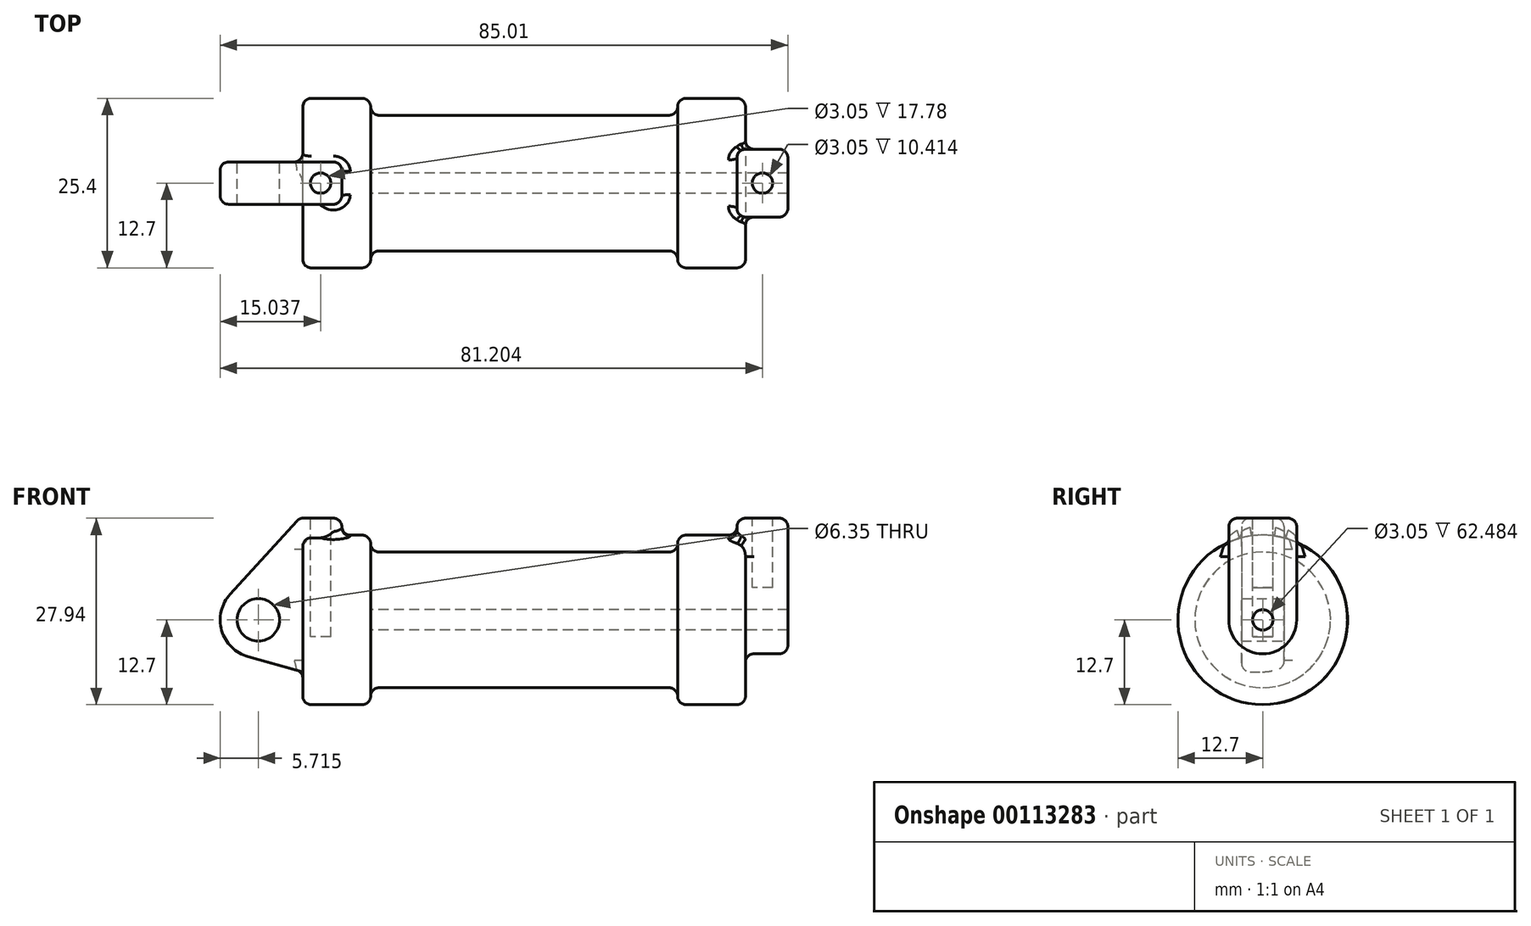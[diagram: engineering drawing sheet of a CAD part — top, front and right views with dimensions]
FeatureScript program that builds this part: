
annotation { "Feature Type Name" : "Feature", "Feature Type Description" : "" }
export const myFeature = defineFeature(function(context is Context, id is Id, definition is map)
    precondition{}
    {
        {
            var Q0;
            Q0=qCreatedBy(makeId("Front.planeOp"),FACE);
            var sketch = newSketch(context, id + "F0", { "sketchPlane" : qUnion([Q0])});
            skLineSegment(sketch, "E0", {"start": v(0, 0) * mm, "end": v(0, 12.7) * mm});
            skLineSegment(sketch, "E1", {"start": v(0, 12.7) * mm, "end": v(10.16, 12.7) * mm});
            skLineSegment(sketch, "E2", {"start": v(10.16, 12.7) * mm, "end": v(10.16, 10.16) * mm});
            skLineSegment(sketch, "E3", {"start": v(10.16, 10.16) * mm, "end": v(56.13, 10.16) * mm});
            skLineSegment(sketch, "E4", {"start": v(56.13, 10.16) * mm, "end": v(56.13, 12.7) * mm});
            skLineSegment(sketch, "E5", {"start": v(56.13, 12.7) * mm, "end": v(66.3, 12.7) * mm});
            skLineSegment(sketch, "E6", {"start": v(66.3, 12.7) * mm, "end": v(66.3, 0) * mm});
            skLineSegment(sketch, "E7", {"start": v(66.3, 0) * mm, "end": v(0, 0) * mm});
            skLineSegment(sketch, "E8", {"start": v(5.84, 15.24) * mm, "end": v(-0.5, 15.24) * mm});
            skLineSegment(sketch, "E9", {"start": v(-0.5, 15.24) * mm, "end": v(-10.88, 3.85) * mm});
            skLineSegment(sketch, "E10", {"start": v(0, 0) * mm, "end": v(-6.65, 0) * mm});
            skCircle(sketch, "E11", {"center": v(-6.65, 0) * mm, "radius": 5.72 * mm});
            skCircle(sketch, "E12", {"center": v(-6.65, 0) * mm, "radius": 3.18 * mm});
            skLineSegment(sketch, "E13", {"start": v(5.84, 15.24) * mm, "end": v(5.84, -9.4) * mm});
            skLineSegment(sketch, "E14", {"start": v(5.84, -9.4) * mm, "end": v(-8.18, -5.5) * mm});
            skSolve(sketch);
        }
        {
            var Q0;
            {var subQ0=sQuery(id+"F0.wireOp",EDGE,"E0");Q0=makeQuery(id+"F0.imprint","IMPRINT",FACE,{"disambiguationData":[TD([[makeQuery(id+"F0.imprint","IMPRINT",EDGE,{"derivedFrom":subQ0}),-1.0]])]});}
            var Q1;
            {var subQ0=sQuery(id+"F0.wireOp",EDGE,"E2");Q1=makeQuery(id+"F0.imprint","IMPRINT",FACE,{"disambiguationData":[TD([[makeQuery(id+"F0.imprint","IMPRINT",EDGE,{"derivedFrom":subQ0}),-1.0]])]});}
            var Q2;
            Q2=sQuery(id+"F0.wireOp",EDGE,"E7");
            revolve(context, id + "F1", {"entities" : qUnion([Q0, Q1]), "axis" : qUnion([Q2]), "revolveType" : RevolveType.FULL});
        }
        {
            var Q0;
            {var subQ0=sQuery(id+"F0.wireOp",EDGE,"E0");Q0=makeQuery(id+"F0.imprint","IMPRINT",FACE,{"disambiguationData":[TD([[makeQuery(id+"F0.imprint","IMPRINT",EDGE,{"derivedFrom":subQ0}),-1.0]])]});}
            var Q1;
            {var subQ3=sQuery(id+"F0.wireOp",EDGE,"E0");Q1=makeQuery(id+"F0.imprint","IMPRINT",FACE,{"disambiguationData":[TD([[makeQuery(id+"F0.imprint","IMPRINT",EDGE,{"derivedFrom":subQ3}),1.0]])]});}
            var Q2;
            {var subQ0=sQuery(id+"F0.wireOp",EDGE,"E14");Q2=makeQuery(id+"F0.imprint","IMPRINT",FACE,{"disambiguationData":[TD([[makeQuery(id+"F0.imprint","IMPRINT",EDGE,{"derivedFrom":subQ0}),-1.0]])]});}
            var Q3;
            {var subQ4=sQuery(id+"F0.wireOp",EDGE,"E12");Q3=makeQuery(id+"F0.imprint","IMPRINT",FACE,{"disambiguationData":[TD([[makeQuery(id+"F0.imprint","IMPRINT",EDGE,{"derivedFrom":subQ4}),-1.0]])]});}
            extrude(context, id + "F2", {"entities" : qUnion([Q0, Q1, Q2, Q3]), "operationType" : NewBodyOperationType.ADD, "endBound" : BoundingType.SYMMETRIC, "depth" : 6.35 * mm});
        }
        {
            var Q0;
            Q0=makeQuery(id+"F1.opRevolve","SWEPT_FACE",FACE,{"disambiguationData":[OSD([sQuery(id+"F0.wireOp",EDGE,"E6")])]});
            var sketch = newSketch(context, id + "F3", { "sketchPlane" : qUnion([Q0])});
            skCircle(sketch, "E15", {"center": v(0, 0) * mm, "radius": 1.52 * mm});
            skCircle(sketch, "E16", {"center": v(0, 0) * mm, "radius": 5.08 * mm});
            skLineSegment(sketch, "E17", {"start": v(-5.08, 0) * mm, "end": v(-5.08, 15.24) * mm});
            skLineSegment(sketch, "E18", {"start": v(-5.08, 15.24) * mm, "end": v(5.08, 15.24) * mm});
            skLineSegment(sketch, "E19", {"start": v(5.08, 15.24) * mm, "end": v(5.08, 0) * mm});
            skSolve(sketch);
        }
        {
            var Q0;
            Q0=makeQuery(id+"F3.imprint","IMPRINT",FACE,{"disambiguationData":[TD([[makeQuery(id+"F3.imprint","IMPRINT",EDGE,{"derivedFrom":sQuery(id+"F3.wireOp",EDGE,"E15")}),-1.0]])]});
            var Q1;
            {var subQ0=sQuery(id+"F3.wireOp",EDGE,"E17");var subQ1=sQuery(id+"F3.wireOp",EDGE,"E16");var subQ2=makeQuery(id+"F3.imprint","INTERSECT",VERTEX,{"derivedFrom":[subQ1,subQ0]});Q1=makeQuery(id+"F3.imprint","IMPRINT",FACE,{"disambiguationData":[TD([[makeQuery(id+"F3.imprint","IMPRINT",EDGE,{"disambiguationData":[TD([[subQ2,1.0]])],"derivedFrom":subQ1}),-1.0]])]});}
            var Q2;
            {var subQ0=sQuery(id+"F3.wireOp",EDGE,"E18");Q2=makeQuery(id+"F3.imprint","IMPRINT",FACE,{"disambiguationData":[TD([[makeQuery(id+"F3.imprint","IMPRINT",EDGE,{"derivedFrom":subQ0}),-1.0]])]});}
            extrude(context, id + "F4", {"entities" : qUnion([Q0, Q1, Q2]), "operationType" : NewBodyOperationType.ADD, "depth" : 6.35 * mm, "hasSecondDirection" : true, "secondDirectionOppositeDirection" : true, "secondDirectionDepth" : 1.27 * mm});
        }
        {
            var Q0;
            Q0=makeQuery(id+"F4.boolean.opBoolean","SPLIT",FACE,{"disambiguationData":[TD([makeQuery(id+"F4.opExtrude","SWEPT_FACE",FACE,{"disambiguationData":[OSD([sQuery(id+"F3.wireOp",EDGE,"E15")])]})])],"derivedFrom":makeQuery(id+"F1.opRevolve","SWEPT_FACE",FACE,{"disambiguationData":[OSD([sQuery(id+"F0.wireOp",EDGE,"E6")])]})});
            var Q1;
            Q1=makeQuery(id+"F1.opRevolve","SWEPT_FACE",FACE,{"disambiguationData":[OSD([sQuery(id+"F0.wireOp",EDGE,"E2")])]});
            extrude(context, id + "F5", {"entities" : qUnion([Q0]), "operationType" : NewBodyOperationType.REMOVE, "endBound" : BoundingType.UP_TO_SURFACE, "oppositeDirection" : true, "endBoundEntityFace" : qUnion([Q1]), "depth" : 41.13 * mm});
        }
        {
            var Q0;
            Q0=makeQuery(id+"F2.opExtrude","SWEPT_FACE",FACE,{"disambiguationData":[OSD([sQuery(id+"F0.wireOp",EDGE,"E8")])]});
            var sketch = newSketch(context, id + "F6", { "sketchPlane" : qUnion([Q0])});
            skCircle(sketch, "E20", {"center": v(2.67, 0) * mm, "radius": 1.52 * mm});
            skPoint(sketch, "E20.centerSnap0", {"position": v(5.84, 0) * mm});
            skPoint(sketch, "E20.centerSnap1", {"position": v(2.67, 3.18) * mm});
            skSolve(sketch);
        }
        {
            var Q0;
            Q0=makeQuery(id+"F6.imprint","IMPRINT",FACE,{"disambiguationData":[TD([[makeQuery(id+"F6.imprint","IMPRINT",EDGE,{"derivedFrom":sQuery(id+"F6.wireOp",EDGE,"E20")}),1.0]])]});
            extrude(context, id + "F7", {"entities" : qUnion([Q0]), "operationType" : NewBodyOperationType.REMOVE, "oppositeDirection" : true, "depth" : 17.78 * mm});
        }
        {
            var Q0;
            Q0=makeQuery(id+"F4.opExtrude","SWEPT_FACE",FACE,{"disambiguationData":[OSD([sQuery(id+"F3.wireOp",EDGE,"E18")])]});
            var sketch = newSketch(context, id + "F8", { "sketchPlane" : qUnion([Q0])});
            skCircle(sketch, "E21", {"center": v(68.83, 0) * mm, "radius": 1.52 * mm});
            skPoint(sketch, "E21.centerSnap0", {"position": v(72.64, 0) * mm});
            skPoint(sketch, "E21.centerSnap1", {"position": v(68.83, 5.08) * mm});
            skSolve(sketch);
        }
        {
            var Q0;
            Q0=makeQuery(id+"F8.imprint","IMPRINT",FACE,{"disambiguationData":[TD([[makeQuery(id+"F8.imprint","IMPRINT",EDGE,{"derivedFrom":sQuery(id+"F8.wireOp",EDGE,"E21")}),1.0]])]});
            extrude(context, id + "F9", {"entities" : qUnion([Q0]), "operationType" : NewBodyOperationType.REMOVE, "oppositeDirection" : true, "depth" : 10.4 * mm});
        }
        {
            var Q0;
            Q0=makeQuery(id+"F1.opRevolve","SWEPT_EDGE",EDGE,{"disambiguationData":[OSD([sQuery(id+"F0.wireOp",EDGE,"E5"),sQuery(id+"F0.wireOp",EDGE,"E6")])]});
            var Q1;
            Q1=makeQuery(id+"F1.opRevolve","SWEPT_EDGE",EDGE,{"disambiguationData":[OSD([sQuery(id+"F0.wireOp",EDGE,"E4"),sQuery(id+"F0.wireOp",EDGE,"E5")])]});
            var Q2;
            Q2=makeQuery(id+"F1.opRevolve","SWEPT_EDGE",EDGE,{"disambiguationData":[OSD([sQuery(id+"F0.wireOp",EDGE,"E2"),sQuery(id+"F0.wireOp",EDGE,"E3")])]});
            var Q3;
            Q3=makeQuery(id+"F1.opRevolve","SWEPT_EDGE",EDGE,{"disambiguationData":[OSD([sQuery(id+"F0.wireOp",EDGE,"E1"),sQuery(id+"F0.wireOp",EDGE,"E2")])]});
            var Q4;
            Q4=makeQuery(id+"F1.opRevolve","SWEPT_EDGE",EDGE,{"disambiguationData":[OSD([sQuery(id+"F0.wireOp",EDGE,"E0"),sQuery(id+"F0.wireOp",EDGE,"E1")])]});
            var Q5;
            Q5=makeQuery(id+"F1.opRevolve","SWEPT_EDGE",EDGE,{"disambiguationData":[OSD([sQuery(id+"F0.wireOp",EDGE,"E3"),sQuery(id+"F0.wireOp",EDGE,"E4")])]});
            fillet(context, id + "F10", {"entities" : qUnion([Q0, Q1, Q2, Q3, Q4, Q5]), "radius" : 1.27 * mm, "tangentPropagation" : true, "allowEdgeOverflow" : false});
        }
        {
            var Q0;
            Q0=makeQuery(id+"F2.opExtrude","SWEPT_EDGE",EDGE,{"disambiguationData":[OSD([sQuery(id+"F0.wireOp",EDGE,"E8"),sQuery(id+"F0.wireOp",EDGE,"E13")])]});
            var Q1;
            Q1=makeQuery(id+"F2.opExtrude","SWEPT_EDGE",EDGE,{"disambiguationData":[OSD([sQuery(id+"F0.wireOp",EDGE,"E8"),sQuery(id+"F0.wireOp",EDGE,"E9")])]});
            var Q2;
            Q2=makeQuery(id+"F2.opExtrude","CAP_EDGE",EDGE,{"disambiguationData":[OSD([sQuery(id+"F0.wireOp",EDGE,"E8")])],"isStart":false});
            var Q3;
            Q3=makeQuery(id+"F2.opExtrude","CAP_EDGE",EDGE,{"disambiguationData":[OSD([sQuery(id+"F0.wireOp",EDGE,"E8")])],"isStart":true});
            var Q4;
            Q4=makeQuery(id+"F2.opExtrude","CAP_EDGE",EDGE,{"disambiguationData":[OSD([sQuery(id+"F0.wireOp",EDGE,"E9")])],"isStart":true});
            var Q5;
            Q5=makeQuery(id+"F2.opExtrude","CAP_EDGE",EDGE,{"disambiguationData":[OSD([sQuery(id+"F0.wireOp",EDGE,"E9")])],"isStart":false});
            var Q6;
            Q6=makeQuery(id+"F2.boolean.opBoolean","INTERSECT",EDGE,{"derivedFrom":[makeQuery(id+"F1.opRevolve","SWEPT_FACE",FACE,{"disambiguationData":[OSD([sQuery(id+"F0.wireOp",EDGE,"E0")])]}),makeQuery(id+"F2.opExtrude","CAP_FACE",FACE,{"disambiguationData":[OSD([sQuery(id+"F0.wireOp",EDGE,"E8"),sQuery(id+"F0.wireOp",EDGE,"E9"),sQuery(id+"F0.wireOp",EDGE,"E11"),sQuery(id+"F0.wireOp",EDGE,"E12"),sQuery(id+"F0.wireOp",EDGE,"E13"),sQuery(id+"F0.wireOp",EDGE,"E14")])],"isStart":true})]});
            var Q7;
            Q7=makeQuery(id+"F2.boolean.opBoolean","INTERSECT",EDGE,{"derivedFrom":[makeQuery(id+"F1.opRevolve","SWEPT_FACE",FACE,{"disambiguationData":[OSD([sQuery(id+"F0.wireOp",EDGE,"E1")])]}),makeQuery(id+"F2.opExtrude","SWEPT_FACE",FACE,{"disambiguationData":[OSD([sQuery(id+"F0.wireOp",EDGE,"E13")])]})]});
            var Q8;
            Q8=makeQuery(id+"F2.opExtrude","CAP_EDGE",EDGE,{"disambiguationData":[OSD([sQuery(id+"F0.wireOp",EDGE,"E13")])],"isStart":false});
            var Q9;
            Q9=makeQuery(id+"F2.opExtrude","CAP_EDGE",EDGE,{"disambiguationData":[OSD([sQuery(id+"F0.wireOp",EDGE,"E13")])],"isStart":true});
            fillet(context, id + "F11", {"entities" : qUnion([Q0, Q1, Q2, Q3, Q4, Q5, Q6, Q7, Q8, Q9]), "radius" : 1.27 * mm, "tangentPropagation" : true, "allowEdgeOverflow" : false});
        }
        {
            var Q0;
            Q0=makeQuery(id+"F4.opExtrude","SWEPT_EDGE",EDGE,{"disambiguationData":[OSD([sQuery(id+"F3.wireOp",EDGE,"E17"),sQuery(id+"F3.wireOp",EDGE,"E18")])]});
            var Q1;
            Q1=makeQuery(id+"F4.opExtrude","CAP_EDGE",EDGE,{"disambiguationData":[OSD([sQuery(id+"F3.wireOp",EDGE,"E18")])],"isStart":false});
            var Q2;
            Q2=makeQuery(id+"F4.opExtrude","SWEPT_EDGE",EDGE,{"disambiguationData":[OSD([sQuery(id+"F3.wireOp",EDGE,"E18"),sQuery(id+"F3.wireOp",EDGE,"E19")])]});
            var Q3;
            Q3=makeQuery(id+"F4.opExtrude","CAP_EDGE",EDGE,{"disambiguationData":[OSD([sQuery(id+"F3.wireOp",EDGE,"E18")])],"isStart":true});
            var Q4;
            Q4=makeQuery(id+"F4.opExtrude","CAP_EDGE",EDGE,{"disambiguationData":[OSD([sQuery(id+"F3.wireOp",EDGE,"E17")])],"isStart":false});
            var Q5;
            Q5=makeQuery(id+"F4.boolean.opBoolean","INTERSECT",EDGE,{"derivedFrom":[makeQuery(id+"F1.opRevolve","SWEPT_FACE",FACE,{"disambiguationData":[OSD([sQuery(id+"F0.wireOp",EDGE,"E6")])]}),makeQuery(id+"F4.opExtrude","SWEPT_FACE",FACE,{"disambiguationData":[OSD([sQuery(id+"F3.wireOp",EDGE,"E19")])]})]});
            var Q6;
            Q6=makeQuery(id+"F4.boolean.opBoolean","INTERSECT",EDGE,{"derivedFrom":[makeQuery(id+"F1.opRevolve","SWEPT_FACE",FACE,{"disambiguationData":[OSD([sQuery(id+"F0.wireOp",EDGE,"E5")])]}),makeQuery(id+"F4.opExtrude","CAP_FACE",FACE,{"disambiguationData":[OSD([sQuery(id+"F3.wireOp",EDGE,"E15"),sQuery(id+"F3.wireOp",EDGE,"E16"),sQuery(id+"F3.wireOp",EDGE,"E17"),sQuery(id+"F3.wireOp",EDGE,"E18"),sQuery(id+"F3.wireOp",EDGE,"E19")])],"isStart":true})]});
            var Q7;
            Q7=makeQuery(id+"F4.opExtrude","CAP_EDGE",EDGE,{"disambiguationData":[OSD([sQuery(id+"F3.wireOp",EDGE,"E17")])],"isStart":true});
            var Q8;
            Q8=makeQuery(id+"F4.opExtrude","CAP_EDGE",EDGE,{"disambiguationData":[OSD([sQuery(id+"F3.wireOp",EDGE,"E19")])],"isStart":true});
            fillet(context, id + "F12", {"entities" : qUnion([Q0, Q1, Q2, Q3, Q4, Q5, Q6, Q7, Q8]), "radius" : 1.27 * mm, "tangentPropagation" : true, "allowEdgeOverflow" : false});
        }
    });
